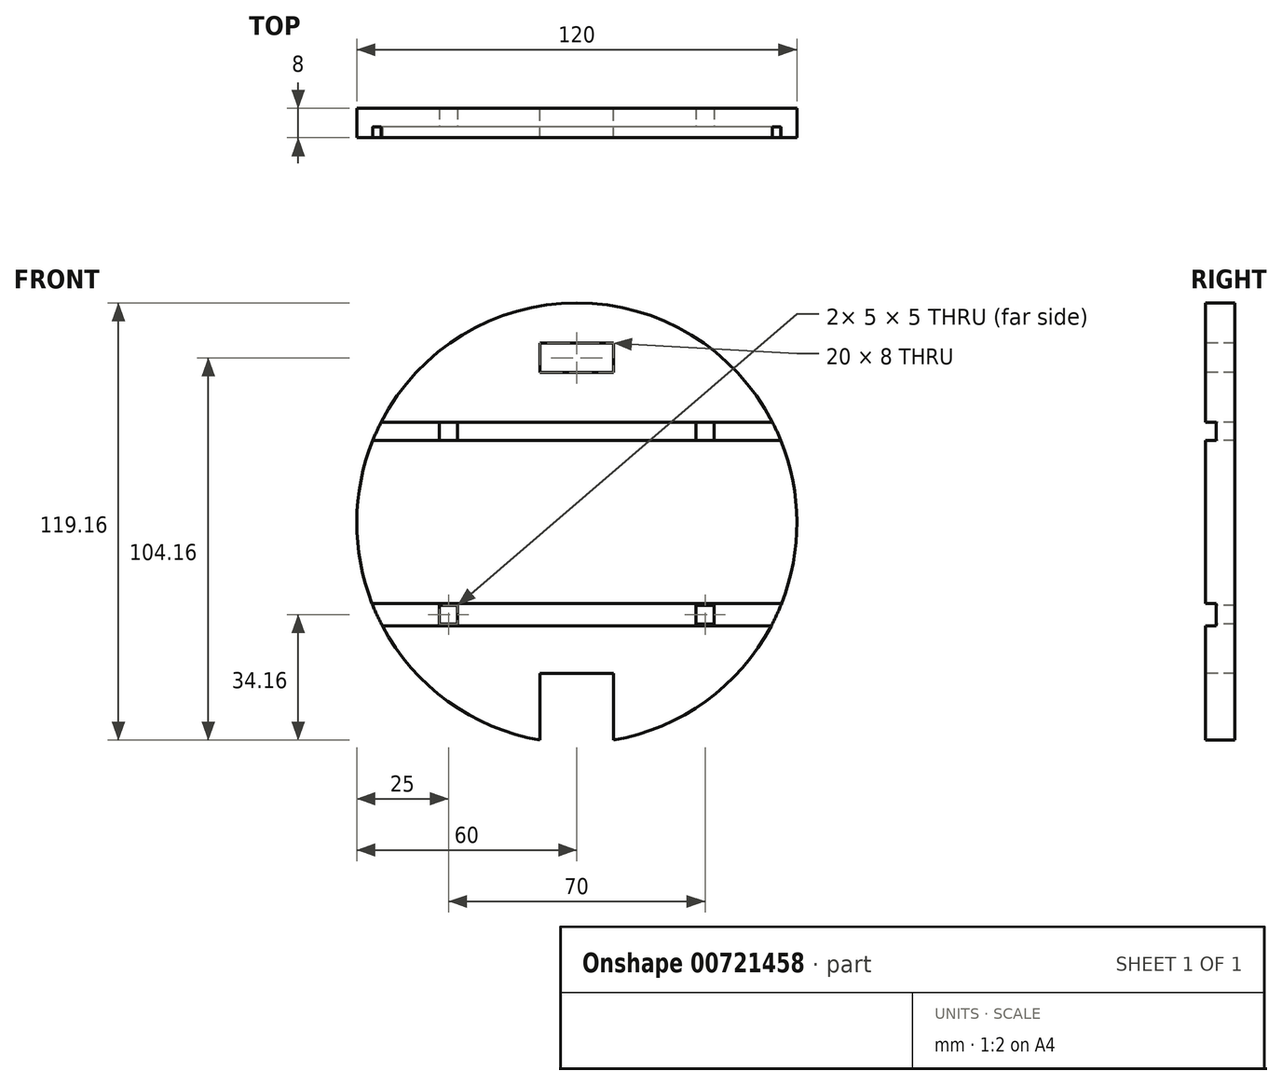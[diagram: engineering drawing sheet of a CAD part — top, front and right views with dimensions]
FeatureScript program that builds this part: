
annotation { "Feature Type Name" : "Feature", "Feature Type Description" : "" }
export const myFeature = defineFeature(function(context is Context, id is Id, definition is map)
    precondition{}
    {
        {
            var Q0;
            Q0=qCreatedBy(makeId("Front.planeOp"),FACE);
            var sketch = newSketch(context, id + "F0", { "sketchPlane" : qUnion([Q0])});
            skCircle(sketch, "E0", {"center": v(0, 0) * mm, "radius": 60 * mm});
            skSolve(sketch);
        }
        {
            var Q0;
            Q0=makeQuery(id+"F0.imprint","IMPRINT",FACE,{"disambiguationData":[TD([[makeQuery(id+"F0.imprint","IMPRINT",EDGE,{"derivedFrom":sQuery(id+"F0.wireOp",EDGE,"E0")}),1.0]])]});
            extrude(context, id + "F1", {"entities" : qUnion([Q0]), "depth" : 8 * mm, "offsetDistance" : 25.4 * mm});
        }
        {
            var Q0;
            Q0=makeQuery(id+"F1.opExtrude","CAP_FACE",FACE,{"disambiguationData":[OSD([sQuery(id+"F0.wireOp",EDGE,"E0")])],"isStart":false});
            var sketch = newSketch(context, id + "F2", { "sketchPlane" : qUnion([Q0])});
            skLineSegment(sketch, "E1.bottom", {"start": v(35, 25) * mm, "end": v(-35, 25) * mm});
            skLineSegment(sketch, "E1.top", {"start": v(35, -25) * mm, "end": v(-35, -25) * mm});
            skLineSegment(sketch, "E1.left", {"start": v(35, 25) * mm, "end": v(35, -25) * mm});
            skLineSegment(sketch, "E1.right", {"start": v(-35, 25) * mm, "end": v(-35, -25) * mm});
            skPoint(sketch, "E1.middle", {"position": v(0, 0) * mm});
            skLineSegment(sketch, "E2.bottom", {"start": v(60, 27.5) * mm, "end": v(-60, 27.5) * mm});
            skLineSegment(sketch, "E2.top", {"start": v(60, 22.5) * mm, "end": v(-60, 22.5) * mm});
            skLineSegment(sketch, "E2.left", {"start": v(60, 27.5) * mm, "end": v(60, 22.5) * mm});
            skLineSegment(sketch, "E2.right", {"start": v(-60, 27.5) * mm, "end": v(-60, 22.5) * mm});
            skPoint(sketch, "E2.middle", {"position": v(0, 25) * mm});
            skLineSegment(sketch, "E3.bottom", {"start": v(60, -21.92) * mm, "end": v(-60, -21.92) * mm});
            skLineSegment(sketch, "E3.top", {"start": v(60, -28.08) * mm, "end": v(-60, -28.08) * mm});
            skLineSegment(sketch, "E3.left", {"start": v(60, -21.92) * mm, "end": v(60, -28.08) * mm});
            skLineSegment(sketch, "E3.right", {"start": v(-60, -21.92) * mm, "end": v(-60, -28.08) * mm});
            skPoint(sketch, "E3.middle", {"position": v(0, -25) * mm});
            skPoint(sketch, "E3.cornerSnap0", {"position": v(60, 25) * mm});
            skSolve(sketch);
        }
        {
            var Q0;
            {var subQ5=sQuery(id+"F2.wireOp",EDGE,"E1.bottom");Q0=makeQuery(id+"F2.imprint","IMPRINT",FACE,{"disambiguationData":[TD([[makeQuery(id+"F2.imprint","IMPRINT",EDGE,{"derivedFrom":subQ5}),-1.0]])]});}
            var Q1;
            {var subQ0=sQuery(id+"F2.wireOp",EDGE,"E1.bottom");Q1=makeQuery(id+"F2.imprint","IMPRINT",FACE,{"disambiguationData":[TD([[makeQuery(id+"F2.imprint","IMPRINT",EDGE,{"derivedFrom":subQ0}),1.0]])]});}
            var Q2;
            {var subQ1=sQuery(id+"F2.wireOp",EDGE,"E1.top");Q2=makeQuery(id+"F2.imprint","IMPRINT",FACE,{"disambiguationData":[TD([[makeQuery(id+"F2.imprint","IMPRINT",EDGE,{"derivedFrom":subQ1}),1.0]])]});}
            var Q3;
            {var subQ0=sQuery(id+"F2.wireOp",EDGE,"E1.top");Q3=makeQuery(id+"F2.imprint","IMPRINT",FACE,{"disambiguationData":[TD([[makeQuery(id+"F2.imprint","IMPRINT",EDGE,{"derivedFrom":subQ0}),-1.0]])]});}
            extrude(context, id + "F3", {"entities" : qUnion([Q0, Q1, Q2, Q3]), "operationType" : NewBodyOperationType.REMOVE, "oppositeDirection" : true, "depth" : 3 * mm, "offsetDistance" : 25.4 * mm});
        }
        {
            var Q0;
            {var subQ0=sQuery(id+"F0.wireOp",EDGE,"E0");Q0=makeQuery(id+"F3.boolean.opBoolean","SPLIT",FACE,{"disambiguationData":[TD([makeQuery(id+"F3.opExtrude","SWEPT_FACE",FACE,{"disambiguationData":[OSD([sQuery(id+"F2.wireOp",EDGE,"E2.top")])]})])],"derivedFrom":makeQuery(id+"F1.opExtrude","CAP_FACE",FACE,{"disambiguationData":[OSD([subQ0])],"isStart":false})});}
            var sketch = newSketch(context, id + "F4", { "sketchPlane" : qUnion([Q0])});
            skLineSegment(sketch, "E4.bottom", {"start": v(35, 25) * mm, "end": v(-35, 25) * mm});
            skLineSegment(sketch, "E4.top", {"start": v(35, -25) * mm, "end": v(-35, -25) * mm});
            skLineSegment(sketch, "E4.left", {"start": v(35, 25) * mm, "end": v(35, -25) * mm});
            skLineSegment(sketch, "E4.right", {"start": v(-35, 25) * mm, "end": v(-35, -25) * mm});
            skPoint(sketch, "E4.middle", {"position": v(0, 0) * mm});
            skLineSegment(sketch, "E5.bottom", {"start": v(-32.5, 27.5) * mm, "end": v(-37.5, 27.5) * mm});
            skLineSegment(sketch, "E5.top", {"start": v(-32.5, 22.5) * mm, "end": v(-37.5, 22.5) * mm});
            skLineSegment(sketch, "E5.left", {"start": v(-32.5, 27.5) * mm, "end": v(-32.5, 22.5) * mm});
            skLineSegment(sketch, "E5.right", {"start": v(-37.5, 27.5) * mm, "end": v(-37.5, 22.5) * mm});
            skPoint(sketch, "E5.middle", {"position": v(-35, 25) * mm});
            skLineSegment(sketch, "E6.bottom", {"start": v(-32.5, -22.5) * mm, "end": v(-37.5, -22.5) * mm});
            skLineSegment(sketch, "E6.top", {"start": v(-32.5, -27.5) * mm, "end": v(-37.5, -27.5) * mm});
            skLineSegment(sketch, "E6.left", {"start": v(-32.5, -22.5) * mm, "end": v(-32.5, -27.5) * mm});
            skLineSegment(sketch, "E6.right", {"start": v(-37.5, -22.5) * mm, "end": v(-37.5, -27.5) * mm});
            skPoint(sketch, "E6.middle", {"position": v(-35, -25) * mm});
            skLineSegment(sketch, "E7.bottom", {"start": v(37.5, 27.5) * mm, "end": v(32.5, 27.5) * mm});
            skLineSegment(sketch, "E7.top", {"start": v(37.5, 22.5) * mm, "end": v(32.5, 22.5) * mm});
            skLineSegment(sketch, "E7.left", {"start": v(37.5, 27.5) * mm, "end": v(37.5, 22.5) * mm});
            skLineSegment(sketch, "E7.right", {"start": v(32.5, 27.5) * mm, "end": v(32.5, 22.5) * mm});
            skPoint(sketch, "E7.middle", {"position": v(35, 25) * mm});
            skLineSegment(sketch, "E8.bottom", {"start": v(37.5, -27.5) * mm, "end": v(32.5, -27.5) * mm});
            skLineSegment(sketch, "E8.top", {"start": v(37.5, -22.5) * mm, "end": v(32.5, -22.5) * mm});
            skLineSegment(sketch, "E8.left", {"start": v(37.5, -27.5) * mm, "end": v(37.5, -22.5) * mm});
            skLineSegment(sketch, "E8.right", {"start": v(32.5, -27.5) * mm, "end": v(32.5, -22.5) * mm});
            skPoint(sketch, "E8.middle", {"position": v(35, -25) * mm});
            skSolve(sketch);
        }
        {
            var Q0;
            {var subQ4=sQuery(id+"F4.wireOp",EDGE,"E5.bottom");Q0=makeQuery(id+"F4.imprint","IMPRINT",FACE,{"disambiguationData":[TD([[makeQuery(id+"F4.imprint","IMPRINT",EDGE,{"derivedFrom":subQ4}),1.0]])]});}
            var Q1;
            {var subQ0=sQuery(id+"F4.wireOp",EDGE,"E4.right");var subQ1=sQuery(id+"F4.wireOp",EDGE,"E4.bottom");var subQ2=makeQuery(id+"F4.imprint","INTERSECT",VERTEX,{"derivedFrom":[subQ1,subQ0]});Q1=makeQuery(id+"F4.imprint","IMPRINT",FACE,{"disambiguationData":[TD([[makeQuery(id+"F4.imprint","IMPRINT",EDGE,{"disambiguationData":[TD([[subQ2,1.0]])],"derivedFrom":subQ1}),1.0]])]});}
            var Q2;
            {var subQ4=sQuery(id+"F4.wireOp",EDGE,"E7.bottom");Q2=makeQuery(id+"F4.imprint","IMPRINT",FACE,{"disambiguationData":[TD([[makeQuery(id+"F4.imprint","IMPRINT",EDGE,{"derivedFrom":subQ4}),1.0]])]});}
            var Q3;
            {var subQ0=sQuery(id+"F4.wireOp",EDGE,"E4.left");var subQ1=sQuery(id+"F4.wireOp",EDGE,"E4.bottom");var subQ2=makeQuery(id+"F4.imprint","INTERSECT",VERTEX,{"derivedFrom":[subQ1,subQ0]});Q3=makeQuery(id+"F4.imprint","IMPRINT",FACE,{"disambiguationData":[TD([[makeQuery(id+"F4.imprint","IMPRINT",EDGE,{"disambiguationData":[TD([[subQ2,-1.0]])],"derivedFrom":subQ1}),1.0]])]});}
            var Q4;
            {var subQ0=sQuery(id+"F4.wireOp",EDGE,"E8.bottom");Q4=makeQuery(id+"F4.imprint","IMPRINT",FACE,{"disambiguationData":[TD([[makeQuery(id+"F4.imprint","IMPRINT",EDGE,{"derivedFrom":subQ0}),-1.0]])]});}
            var Q5;
            {var subQ0=sQuery(id+"F4.wireOp",EDGE,"E4.left");var subQ1=sQuery(id+"F4.wireOp",EDGE,"E4.top");var subQ2=makeQuery(id+"F4.imprint","INTERSECT",VERTEX,{"derivedFrom":[subQ1,subQ0]});Q5=makeQuery(id+"F4.imprint","IMPRINT",FACE,{"disambiguationData":[TD([[makeQuery(id+"F4.imprint","IMPRINT",EDGE,{"disambiguationData":[TD([[subQ2,-1.0]])],"derivedFrom":subQ1}),-1.0]])]});}
            var Q6;
            {var subQ0=sQuery(id+"F4.wireOp",EDGE,"E6.top");Q6=makeQuery(id+"F4.imprint","IMPRINT",FACE,{"disambiguationData":[TD([[makeQuery(id+"F4.imprint","IMPRINT",EDGE,{"derivedFrom":subQ0}),-1.0]])]});}
            var Q7;
            {var subQ0=sQuery(id+"F4.wireOp",EDGE,"E4.right");var subQ1=sQuery(id+"F4.wireOp",EDGE,"E4.top");var subQ2=makeQuery(id+"F4.imprint","INTERSECT",VERTEX,{"derivedFrom":[subQ1,subQ0]});Q7=makeQuery(id+"F4.imprint","IMPRINT",FACE,{"disambiguationData":[TD([[makeQuery(id+"F4.imprint","IMPRINT",EDGE,{"disambiguationData":[TD([[subQ2,1.0]])],"derivedFrom":subQ1}),-1.0]])]});}
            extrude(context, id + "F5", {"entities" : qUnion([Q0, Q1, Q2, Q3, Q4, Q5, Q6, Q7]), "operationType" : NewBodyOperationType.REMOVE, "endBound" : BoundingType.THROUGH_ALL, "oppositeDirection" : true, "depth" : 6 * mm, "offsetDistance" : 25.4 * mm});
        }
        {
            var Q0;
            {var subQ0=sQuery(id+"F0.wireOp",EDGE,"E0");Q0=makeQuery(id+"F3.boolean.opBoolean","SPLIT",FACE,{"disambiguationData":[TD([makeQuery(id+"F3.opExtrude","SWEPT_FACE",FACE,{"disambiguationData":[OSD([sQuery(id+"F2.wireOp",EDGE,"E2.bottom")])]})])],"derivedFrom":makeQuery(id+"F1.opExtrude","CAP_FACE",FACE,{"disambiguationData":[OSD([subQ0])],"isStart":false})});}
            var sketch = newSketch(context, id + "F6", { "sketchPlane" : qUnion([Q0])});
            skLineSegment(sketch, "E9", {"start": v(0, 0) * mm, "end": v(0, 45) * mm});
            skPoint(sketch, "E9.endSnap0", {"position": v(0, 27.5) * mm});
            skLineSegment(sketch, "E10.bottom", {"start": v(10, 49) * mm, "end": v(-10, 49) * mm});
            skLineSegment(sketch, "E10.top", {"start": v(10, 41) * mm, "end": v(-10, 41) * mm});
            skLineSegment(sketch, "E10.left", {"start": v(10, 49) * mm, "end": v(10, 41) * mm});
            skLineSegment(sketch, "E10.right", {"start": v(-10, 49) * mm, "end": v(-10, 41) * mm});
            skPoint(sketch, "E10.middle", {"position": v(0, 45) * mm});
            skLineSegment(sketch, "E11", {"start": v(0, 0) * mm, "end": v(0, -45) * mm});
            skLineSegment(sketch, "E12.bottom", {"start": v(10, -41) * mm, "end": v(-10, -41) * mm});
            skLineSegment(sketch, "E12.top", {"start": v(10, -49) * mm, "end": v(-10, -49) * mm});
            skLineSegment(sketch, "E12.left", {"start": v(10, -41) * mm, "end": v(10, -49) * mm});
            skLineSegment(sketch, "E12.right", {"start": v(-10, -41) * mm, "end": v(-10, -49) * mm});
            skPoint(sketch, "E12.middle", {"position": v(0, -45) * mm});
            skSolve(sketch);
        }
        {
            var Q0;
            Q0=makeQuery(id+"F6.imprint","IMPRINT",FACE,{"disambiguationData":[TD([[makeQuery(id+"F6.imprint","IMPRINT",EDGE,{"derivedFrom":sQuery(id+"F6.wireOp",EDGE,"E10.bottom")}),1.0]])]});
            var Q1;
            Q1=makeQuery(id+"F6.imprint","IMPRINT",FACE,{"disambiguationData":[TD([[makeQuery(id+"F6.imprint","IMPRINT",EDGE,{"derivedFrom":sQuery(id+"F6.wireOp",EDGE,"E12.top")}),-1.0]])]});
            extrude(context, id + "F7", {"entities" : qUnion([Q0, Q1]), "operationType" : NewBodyOperationType.REMOVE, "endBound" : BoundingType.THROUGH_ALL, "oppositeDirection" : true, "depth" : 25.4 * mm, "offsetDistance" : 25.4 * mm});
        }
        {
            var Q0;
            Q0=makeQuery(id+"F1.opExtrude","CAP_FACE",FACE,{"disambiguationData":[OSD([sQuery(id+"F0.wireOp",EDGE,"E0")])],"isStart":true});
            var sketch = newSketch(context, id + "F8", { "sketchPlane" : qUnion([Q0])});
            skLineSegment(sketch, "E13", {"start": v(-10, -49) * mm, "end": v(-10, -59.16) * mm});
            skLineSegment(sketch, "E14", {"start": v(10, -49) * mm, "end": v(10, -59.16) * mm});
            skSolve(sketch);
        }
        {
            var Q0;
            {var subQ0=sQuery(id+"F8.wireOp",EDGE,"E13");Q0=makeQuery(id+"F8.imprint","IMPRINT",FACE,{"disambiguationData":[TD([[makeQuery(id+"F8.imprint","IMPRINT",EDGE,{"derivedFrom":subQ0}),1.0]])]});}
            extrude(context, id + "F9", {"entities" : qUnion([Q0]), "operationType" : NewBodyOperationType.REMOVE, "endBound" : BoundingType.THROUGH_ALL, "oppositeDirection" : true, "depth" : 25.4 * mm, "offsetDistance" : 25.4 * mm});
        }
    });
